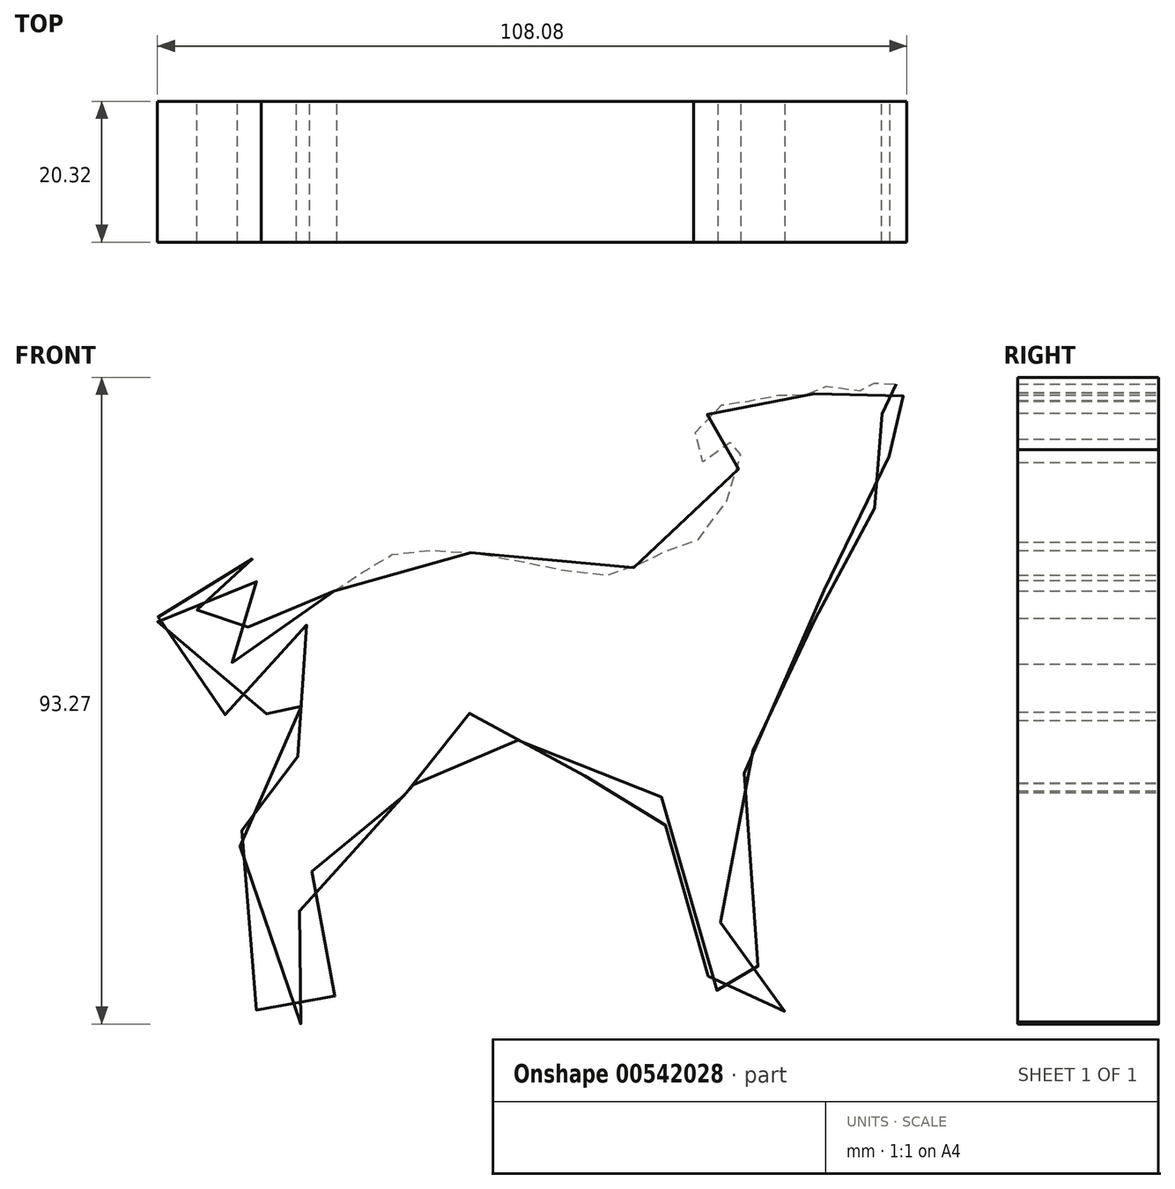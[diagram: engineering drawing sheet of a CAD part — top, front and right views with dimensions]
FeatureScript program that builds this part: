
annotation { "Feature Type Name" : "Feature", "Feature Type Description" : "" }
export const myFeature = defineFeature(function(context is Context, id is Id, definition is map)
    precondition{}
    {
        {
            var Q0;
            Q0=qCreatedBy(makeId("Front.planeOp"),FACE);
            var sketch = newSketch(context, id + "F0", { "sketchPlane" : qUnion([Q0])});
            skFitSpline(sketch, "E0", {"points": [v(-46.63, 10.52) * mm, v(-41.45, 14.17) * mm, v(-35.36, 16.3) * mm, v(-24.38, 15.7) * mm, v(-13.72, 13.56) * mm, v(-4.88, 13.26) * mm, v(0, 16) * mm, v(5.18, 17.53) * mm, v(11.58, 27.89) * mm, v(11.28, 32.46) * mm, v(6.7, 29.1) * mm, v(5.49, 33.68) * mm, v(10.97, 37.95) * mm, v(14.02, 37.95) * mm, v(19.81, 39.17) * mm, v(22.25, 38.86) * mm, v(25.6, 40.39) * mm, v(30.78, 39.17) * mm, v(31.4, 41) * mm, v(35.05, 39.47) * mm, v(34.75, 30.94) * mm, v(32.3, 36.12) * mm, v(33.22, 30.94) * mm, v(32.3, 23.62) * mm, v(27.13, 18.75) * mm, v(22.86, 6.86) * mm, v(17.07, -5.64) * mm, v(10.97, -20.27) * mm, v(9.75, -39.47) * mm, v(16.15, -44.96) * mm, v(17.98, -50.75) * mm, v(11.89, -50.75) * mm, v(7.62, -45.57) * mm, v(2.44, -34.9) * mm, v(0, -17.83) * mm, v(-3.35, -17.22) * mm, v(-15.54, -14.17) * mm, v(-24.38, -8.08) * mm, v(-31.09, -7.77) * mm, v(-34.75, -16.61) * mm, v(-41.45, -22.1) * mm, v(-48.46, -27.28) * mm, v(-51.2, -43.74) * mm, v(-46.33, -48.31) * mm, v(-48.46, -51.36) * mm, v(-56.7, -50.75) * mm, v(-60.05, -43.74) * mm, v(-57.91, -18.75) * mm, v(-53.64, -18.44) * mm, v(-51.51, -7.16) * mm, v(-50.3, 6.55) * mm, v(-55.47, -6.25) * mm, v(-62.79, -7.16) * mm, v(-70.71, 0) * mm, v(-71.32, 9.6) * mm, v(-62.48, 17.53) * mm, v(-57.3, 12.34) * mm, v(-64.31, 11.13) * mm, v(-66.14, 5.64) * mm, v(-61.87, 0) * mm, v(-58.22, 7.16) * mm, v(-51.2, 12.04) * mm, v(-46.63, 10.52) * mm]});
            skSolve(sketch);
        }
        {
            var Q0;
            Q0 = qSketchRegion(id + "F0", true);
            extrude(context, id + "F1", {"entities" : qUnion([Q0]), "depth" : 20.32 * mm, "offsetDistance" : 25.4 * mm});
        }
    });
